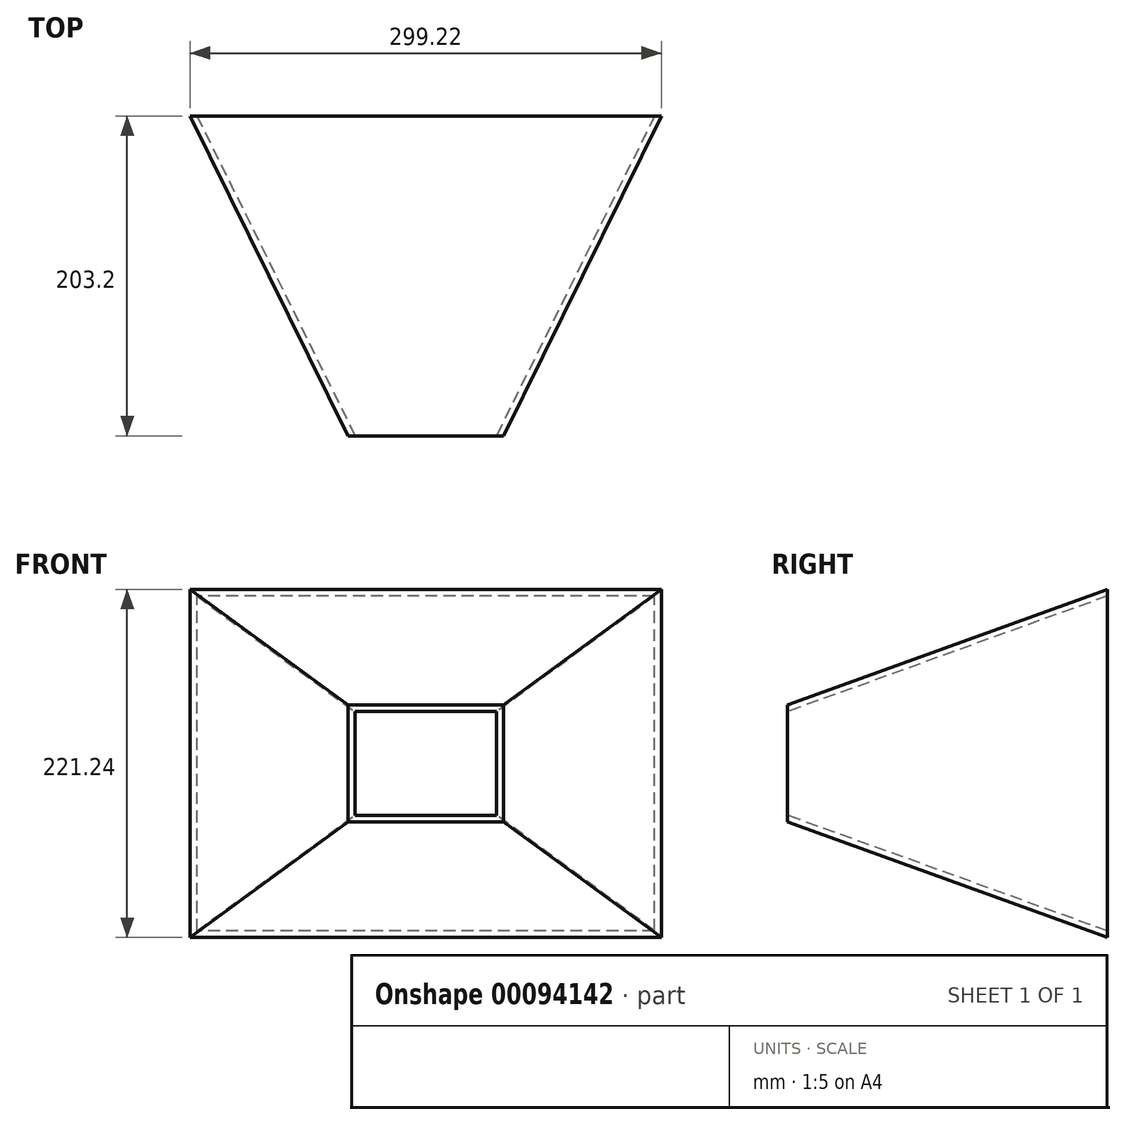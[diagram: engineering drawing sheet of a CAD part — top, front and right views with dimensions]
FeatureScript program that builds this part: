
annotation { "Feature Type Name" : "Feature", "Feature Type Description" : "" }
export const myFeature = defineFeature(function(context is Context, id is Id, definition is map)
    precondition{}
    {
        {
            var Q0;
            Q0=qCreatedBy(makeId("Front.planeOp"),FACE);
            var sketch = newSketch(context, id + "F0", { "sketchPlane" : qUnion([Q0])});
            skLineSegment(sketch, "E0.bottom", {"start": v(149.6, 110.62) * mm, "end": v(-149.6, 110.62) * mm});
            skLineSegment(sketch, "E0.top", {"start": v(149.6, -110.62) * mm, "end": v(-149.6, -110.62) * mm});
            skLineSegment(sketch, "E0.left", {"start": v(149.6, 110.62) * mm, "end": v(149.6, -110.62) * mm});
            skLineSegment(sketch, "E0.right", {"start": v(-149.6, 110.62) * mm, "end": v(-149.6, -110.62) * mm});
            skPoint(sketch, "E0.middle", {"position": v(0, 0) * mm});
            skPoint(sketch, "E1.left.start.orphan", {"position": v(143.13, 104.14) * mm});
            skPoint(sketch, "E1.top.start.orphan", {"position": v(143.13, -104.14) * mm});
            skPoint(sketch, "E1.right.end.orphan", {"position": v(-143.13, -104.14) * mm});
            skPoint(sketch, "E1.right.start.orphan", {"position": v(-143.13, 104.14) * mm});
            skSolve(sketch);
        }
        {
            var Q0;
            Q0=makeQuery(id+"F0.imprint","IMPRINT",FACE,{"disambiguationData":[TD([[makeQuery(id+"F0.imprint","IMPRINT",EDGE,{"derivedFrom":sQuery(id+"F0.wireOp",EDGE,"E0.bottom")}),1.0]])]});
            cPlane(context, id + "F1", {"entities" : qUnion([Q0]), "cplaneType" : CPlaneType.OFFSET, "offset" : 203.2 * mm, "width" : 152.4 * mm, "height" : 152.4 * mm});
        }
        {
            var Q0;
            Q0=qCreatedBy(id+"F1.planeOp",FACE);
            var sketch = newSketch(context, id + "F2", { "sketchPlane" : qUnion([Q0])});
            skLineSegment(sketch, "E2.bottom", {"start": v(-49.28, 37.21) * mm, "end": v(49.28, 37.21) * mm});
            skLineSegment(sketch, "E2.top", {"start": v(-49.28, -37.21) * mm, "end": v(49.28, -37.21) * mm});
            skLineSegment(sketch, "E2.left", {"start": v(-49.28, 37.21) * mm, "end": v(-49.28, -37.21) * mm});
            skLineSegment(sketch, "E2.right", {"start": v(49.28, 37.21) * mm, "end": v(49.28, -37.21) * mm});
            skPoint(sketch, "E2.middle", {"position": v(0, 0) * mm});
            skSolve(sketch);
        }
        {
            var Q0;
            Q0=makeQuery(id+"F2.imprint","IMPRINT",FACE,{"disambiguationData":[TD([[makeQuery(id+"F2.imprint","IMPRINT",EDGE,{"derivedFrom":sQuery(id+"F2.wireOp",EDGE,"E2.bottom")}),-1.0]])]});
            var Q1;
            Q1=makeQuery(id+"F0.imprint","IMPRINT",FACE,{"disambiguationData":[TD([[makeQuery(id+"F0.imprint","IMPRINT",EDGE,{"derivedFrom":sQuery(id+"F0.wireOp",EDGE,"E0.bottom")}),1.0]])]});
            loft(context, id + "F3", {"sheetProfilesArray" : [{ "sheetProfileEntities" : qUnion([Q0]) }, { "sheetProfileEntities" : qUnion([Q1]) }]});
        }
        {
            var Q0;
            Q0=makeQuery(id+"F3.opLoft","CAP_FACE",FACE,{"disambiguationData":[OSD([makeQuery(id+"F2.imprint","IMPRINT",FACE,{"disambiguationData":[TD([[makeQuery(id+"F2.imprint","IMPRINT",EDGE,{"derivedFrom":sQuery(id+"F2.wireOp",EDGE,"E2.bottom")}),-1.0]])]})])],"isStart":true});
            var sketch = newSketch(context, id + "F4", { "sketchPlane" : qUnion([Q0])});
            skLineSegment(sketch, "E3.bottom", {"start": v(44.96, -32.9) * mm, "end": v(-44.96, -32.9) * mm});
            skLineSegment(sketch, "E3.top", {"start": v(44.96, 32.9) * mm, "end": v(-44.96, 32.9) * mm});
            skLineSegment(sketch, "E3.left", {"start": v(44.96, -32.9) * mm, "end": v(44.96, 32.9) * mm});
            skLineSegment(sketch, "E3.right", {"start": v(-44.96, -32.9) * mm, "end": v(-44.96, 32.9) * mm});
            skPoint(sketch, "E3.middle", {"position": v(0, 0) * mm});
            skSolve(sketch);
        }
        {
            var Q0;
            Q0=makeQuery(id+"F3.opLoft","CAP_FACE",FACE,{"disambiguationData":[OSD([makeQuery(id+"F0.imprint","IMPRINT",FACE,{"disambiguationData":[TD([[makeQuery(id+"F0.imprint","IMPRINT",EDGE,{"derivedFrom":sQuery(id+"F0.wireOp",EDGE,"E0.bottom")}),1.0]])]})])],"isStart":true});
            var sketch = newSketch(context, id + "F5", { "sketchPlane" : qUnion([Q0])});
            skLineSegment(sketch, "E4.bottom", {"start": v(-145.29, -106.3) * mm, "end": v(145.29, -106.3) * mm});
            skLineSegment(sketch, "E4.top", {"start": v(-145.29, 106.3) * mm, "end": v(145.29, 106.3) * mm});
            skLineSegment(sketch, "E4.left", {"start": v(-145.29, -106.3) * mm, "end": v(-145.29, 106.3) * mm});
            skLineSegment(sketch, "E4.right", {"start": v(145.29, -106.3) * mm, "end": v(145.29, 106.3) * mm});
            skPoint(sketch, "E4.middle", {"position": v(0, 0) * mm});
            skSolve(sketch);
        }
        {
            var Q1;
            Q1=makeQuery(id+"F5.imprint","IMPRINT",FACE,{"disambiguationData":[TD([[makeQuery(id+"F5.imprint","IMPRINT",EDGE,{"derivedFrom":sQuery(id+"F5.wireOp",EDGE,"E4.bottom")}),1.0]])]});
            var Q2;
            Q2=makeQuery(id+"F4.imprint","IMPRINT",FACE,{"disambiguationData":[TD([[makeQuery(id+"F4.imprint","IMPRINT",EDGE,{"derivedFrom":sQuery(id+"F4.wireOp",EDGE,"E3.bottom")}),-1.0]])]});
            loft(context, id + "F6", {"operationType" : NewBodyOperationType.REMOVE, "sheetProfilesArray" : [{ "sheetProfileEntities" : qUnion([Q1]) }, { "sheetProfileEntities" : qUnion([Q2]) }]});
        }
    });
